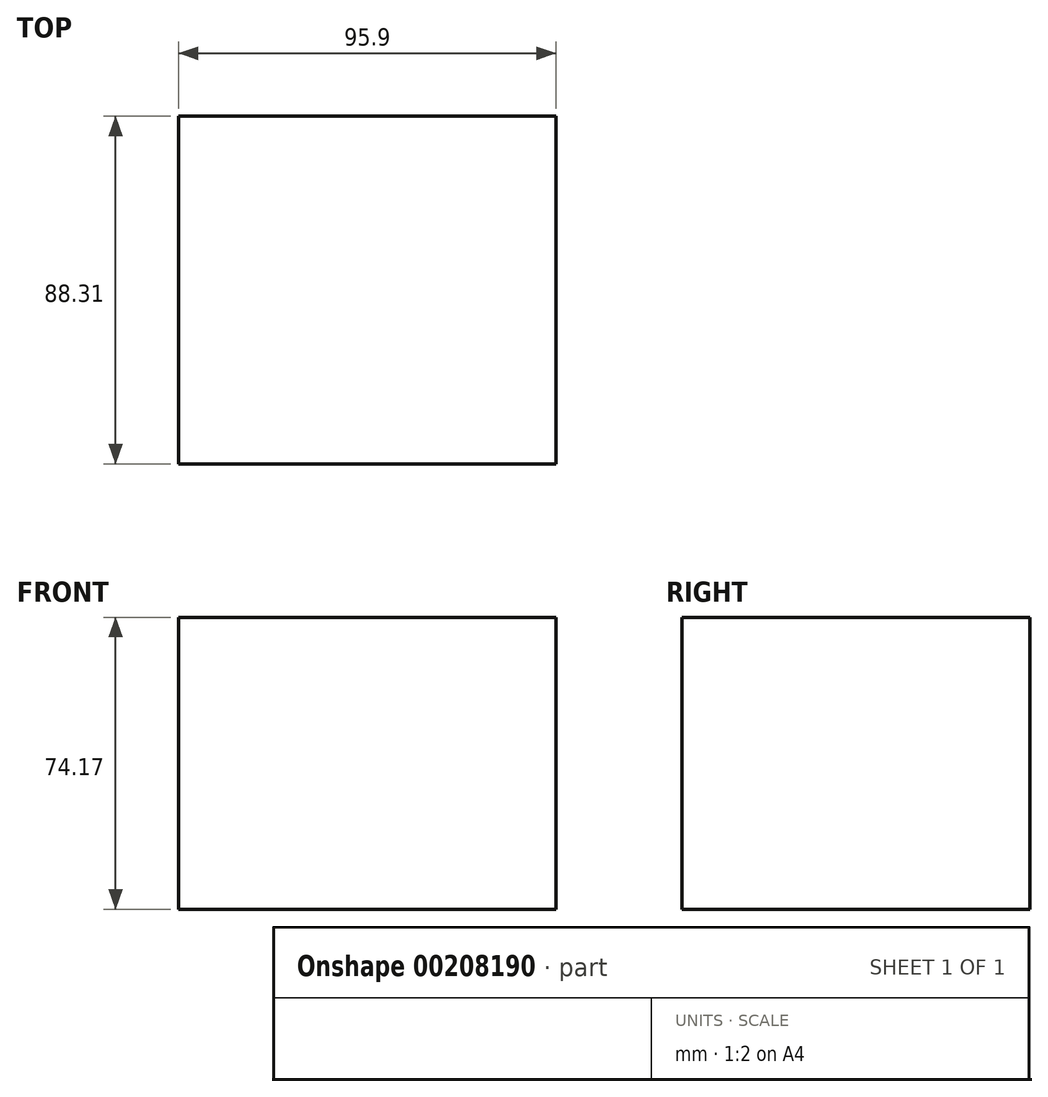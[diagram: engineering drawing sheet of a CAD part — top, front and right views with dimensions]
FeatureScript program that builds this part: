
annotation { "Feature Type Name" : "Feature", "Feature Type Description" : "" }
export const myFeature = defineFeature(function(context is Context, id is Id, definition is map)
    precondition{}
    {
        {
            var Q0;
            Q0=qCreatedBy(makeId("Top.planeOp"),FACE);
            var sketch = newSketch(context, id + "F0", { "sketchPlane" : qUnion([Q0])});
            skLineSegment(sketch, "E0.bottom", {"start": v(46.64, -45.32) * mm, "end": v(-49.26, -45.32) * mm});
            skLineSegment(sketch, "E0.top", {"start": v(46.64, 43) * mm, "end": v(-49.26, 43) * mm});
            skLineSegment(sketch, "E0.left", {"start": v(46.64, -45.32) * mm, "end": v(46.64, 43) * mm});
            skLineSegment(sketch, "E0.right", {"start": v(-49.26, -45.32) * mm, "end": v(-49.26, 43) * mm});
            skSolve(sketch);
        }
        {
            var Q0;
            Q0=makeQuery(id+"F0.imprint","IMPRINT",FACE,{"disambiguationData":[TD([[makeQuery(id+"F0.imprint","IMPRINT",EDGE,{"derivedFrom":sQuery(id+"F0.wireOp",EDGE,"E0.bottom")}),-1.0]])]});
            extrude(context, id + "F1", {"entities" : qUnion([Q0]), "depth" : 74.17 * mm});
        }
    });
